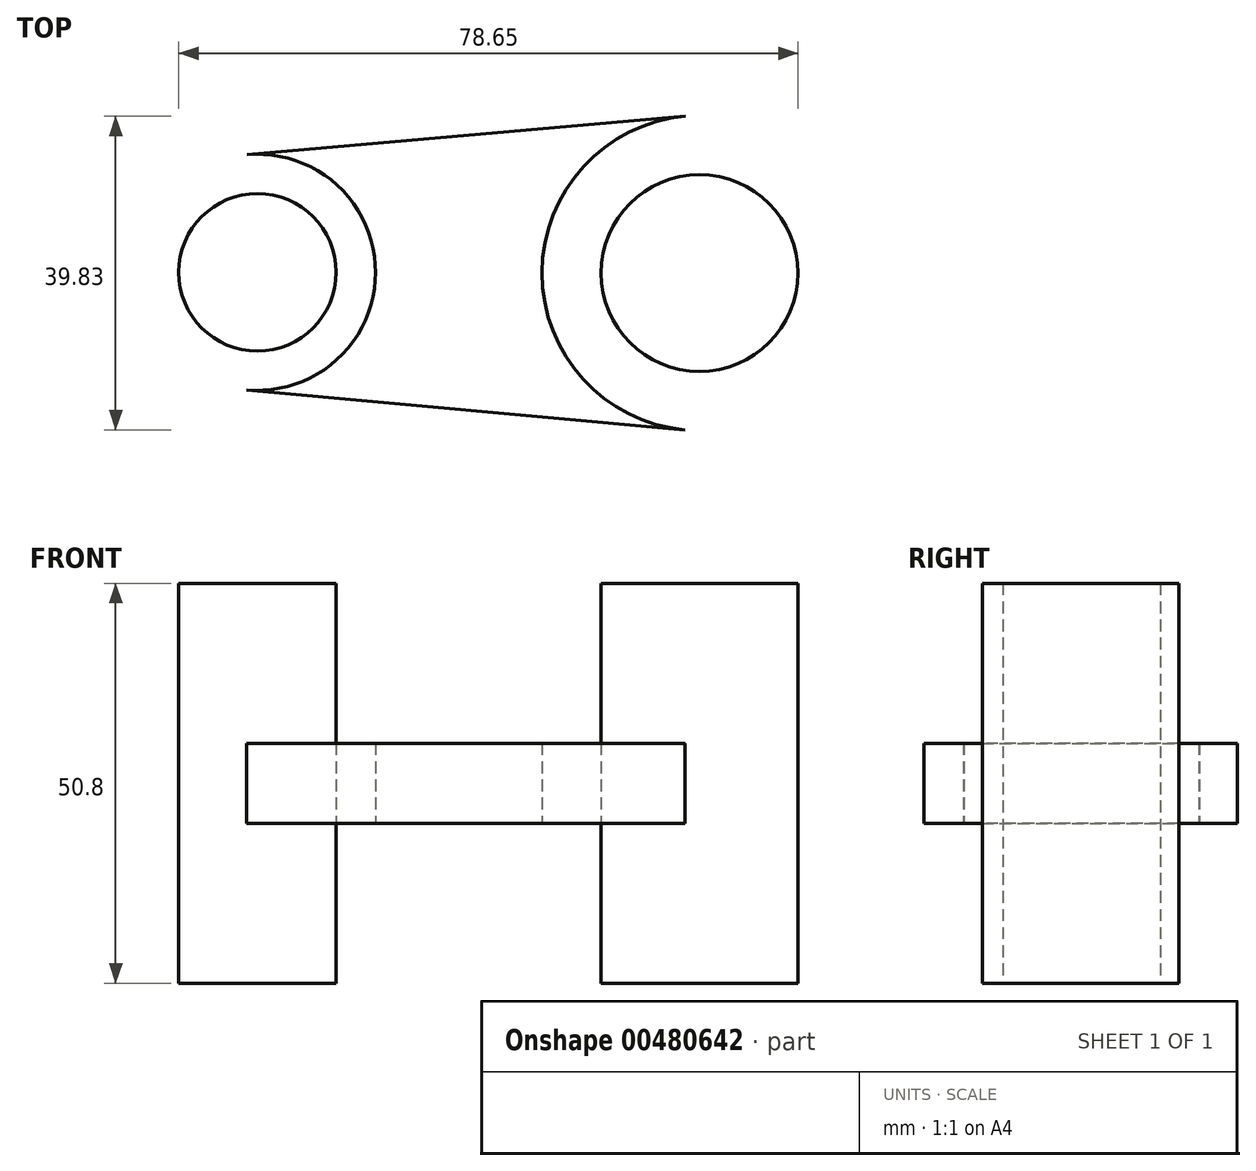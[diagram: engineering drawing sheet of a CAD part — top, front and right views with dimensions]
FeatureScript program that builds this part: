
annotation { "Feature Type Name" : "Feature", "Feature Type Description" : "" }
export const myFeature = defineFeature(function(context is Context, id is Id, definition is map)
    precondition{}
    {
        {
            var Q0;
            Q0=qCreatedBy(makeId("Top.planeOp"),FACE);
            var sketch = newSketch(context, id + "F0", { "sketchPlane" : qUnion([Q0])});
            skCircle(sketch, "E0", {"center": v(-100.83, -7.92) * mm, "radius": 20 * mm});
            skCircle(sketch, "E1", {"center": v(-100.83, -7.92) * mm, "radius": 12.5 * mm});
            skCircle(sketch, "E2", {"center": v(-156.98, -7.82) * mm, "radius": 10 * mm});
            skCircle(sketch, "E3", {"center": v(-156.98, -7.82) * mm, "radius": 15 * mm});
            skLineSegment(sketch, "E4", {"start": v(-102.67, -27.83) * mm, "end": v(-158.35, -22.76) * mm});
            skLineSegment(sketch, "E5", {"start": v(-102.6, 12) * mm, "end": v(-158.3, 7.12) * mm});
            skLineSegment(sketch, "E6", {"start": v(-156.98, -7.82) * mm, "end": v(-211.76, -7.82) * mm});
            skLineSegment(sketch, "E7", {"start": v(-211.76, -7.82) * mm, "end": v(211.76, -7.82) * mm, "construction": true});
            skLineSegment(sketch, "E8", {"start": v(0, -7.82) * mm, "end": v(0, -17.82) * mm});
            skLineSegment(sketch, "E9", {"start": v(0, -17.82) * mm, "end": v(0, 2.18) * mm});
            skLineSegment(sketch, "E10", {"start": v(0, 2.18) * mm, "end": v(30, 2.18) * mm});
            skLineSegment(sketch, "E11", {"start": v(30, -17.82) * mm, "end": v(0, -17.82) * mm});
            skLineSegment(sketch, "E12", {"start": v(15, -5.82) * mm, "end": v(15, -9.82) * mm});
            skLineSegment(sketch, "E13", {"start": v(15, -9.82) * mm, "end": v(70.69, -9.82) * mm});
            skLineSegment(sketch, "E14", {"start": v(70.69, -9.82) * mm, "end": v(70.69, -5.82) * mm});
            skLineSegment(sketch, "E15", {"start": v(70.69, -5.82) * mm, "end": v(15, -5.82) * mm});
            skLineSegment(sketch, "E16", {"start": v(30, 2.18) * mm, "end": v(30, -5.82) * mm});
            skLineSegment(sketch, "E17", {"start": v(30, -17.82) * mm, "end": v(30, -9.82) * mm});
            skLineSegment(sketch, "E18", {"start": v(90.69, -7.82) * mm, "end": v(90.69, 12.18) * mm});
            skLineSegment(sketch, "E19", {"start": v(90.69, 12.18) * mm, "end": v(50.69, 12.18) * mm});
            skLineSegment(sketch, "E20", {"start": v(50.69, -27.82) * mm, "end": v(90.69, -27.82) * mm});
            skLineSegment(sketch, "E21", {"start": v(90.69, -27.82) * mm, "end": v(90.69, -7.82) * mm});
            skLineSegment(sketch, "E22", {"start": v(50.69, 12.18) * mm, "end": v(50.69, -5.82) * mm});
            skLineSegment(sketch, "E23", {"start": v(50.69, -27.82) * mm, "end": v(50.69, -9.82) * mm});
            skLineSegment(sketch, "E24", {"start": v(15, -7.82) * mm, "end": v(15, 21.98) * mm});
            skLineSegment(sketch, "E25", {"start": v(15, 21.98) * mm, "end": v(15, -36.17) * mm, "construction": true});
            skLineSegment(sketch, "E26", {"start": v(70.69, -7.82) * mm, "end": v(70.69, 22.85) * mm});
            skLineSegment(sketch, "E27", {"start": v(70.69, 22.85) * mm, "end": v(70.69, -35.47) * mm, "construction": true});
            skLineSegment(sketch, "E28", {"start": v(5, -7.82) * mm, "end": v(5, -17.82) * mm, "construction": true});
            skLineSegment(sketch, "E29", {"start": v(5, -17.82) * mm, "end": v(25, -17.82) * mm});
            skLineSegment(sketch, "E30", {"start": v(25, -17.82) * mm, "end": v(25, 2.18) * mm, "construction": true});
            skLineSegment(sketch, "E31", {"start": v(25, 2.18) * mm, "end": v(5, 2.18) * mm});
            skLineSegment(sketch, "E32", {"start": v(5, 2.18) * mm, "end": v(5, -7.82) * mm, "construction": true});
            skLineSegment(sketch, "E33", {"start": v(83.19, -7.82) * mm, "end": v(83.19, 12.18) * mm, "construction": true});
            skLineSegment(sketch, "E34", {"start": v(83.19, 12.18) * mm, "end": v(70.69, 12.18) * mm});
            skLineSegment(sketch, "E35", {"start": v(70.69, 12.18) * mm, "end": v(58.19, 12.18) * mm});
            skLineSegment(sketch, "E36", {"start": v(58.19, 12.18) * mm, "end": v(58.19, -27.82) * mm, "construction": true});
            skLineSegment(sketch, "E37", {"start": v(58.19, -27.82) * mm, "end": v(83.19, -27.82) * mm});
            skLineSegment(sketch, "E38", {"start": v(83.19, -27.82) * mm, "end": v(83.19, -7.82) * mm, "construction": true});
            skSolve(sketch);
        }
        {
            var Q0;
            Q0=makeQuery(id+"F0.imprint","IMPRINT",FACE,{"disambiguationData":[TD([[makeQuery(id+"F0.imprint","IMPRINT",EDGE,{"derivedFrom":sQuery(id+"F0.wireOp",EDGE,"E2")}),1.0]])]});
            extrude(context, id + "F1", {"entities" : qUnion([Q0]), "depth" : 25.4 * mm, "hasSecondDirection" : true, "secondDirectionOppositeDirection" : true, "secondDirectionDepth" : 25.4 * mm});
        }
        {
            var Q0;
            {var subQ0=sQuery(id+"F0.wireOp",EDGE,"E4");Q0=makeQuery(id+"F0.imprint","IMPRINT",FACE,{"disambiguationData":[TD([[makeQuery(id+"F0.imprint","IMPRINT",EDGE,{"derivedFrom":subQ0}),-1.0]])]});}
            extrude(context, id + "F2", {"entities" : qUnion([Q0]), "operationType" : NewBodyOperationType.ADD, "depth" : 5.08 * mm, "hasSecondDirection" : true, "secondDirectionOppositeDirection" : true, "secondDirectionDepth" : 5.08 * mm});
        }
        {
            var Q0;
            Q0=makeQuery(id+"F0.imprint","IMPRINT",FACE,{"disambiguationData":[TD([[makeQuery(id+"F0.imprint","IMPRINT",EDGE,{"derivedFrom":sQuery(id+"F0.wireOp",EDGE,"E1")}),1.0]])]});
            extrude(context, id + "F3", {"entities" : qUnion([Q0]), "operationType" : NewBodyOperationType.ADD, "depth" : 25.4 * mm, "hasSecondDirection" : true, "secondDirectionOppositeDirection" : true, "secondDirectionDepth" : 25.4 * mm});
        }
    });
